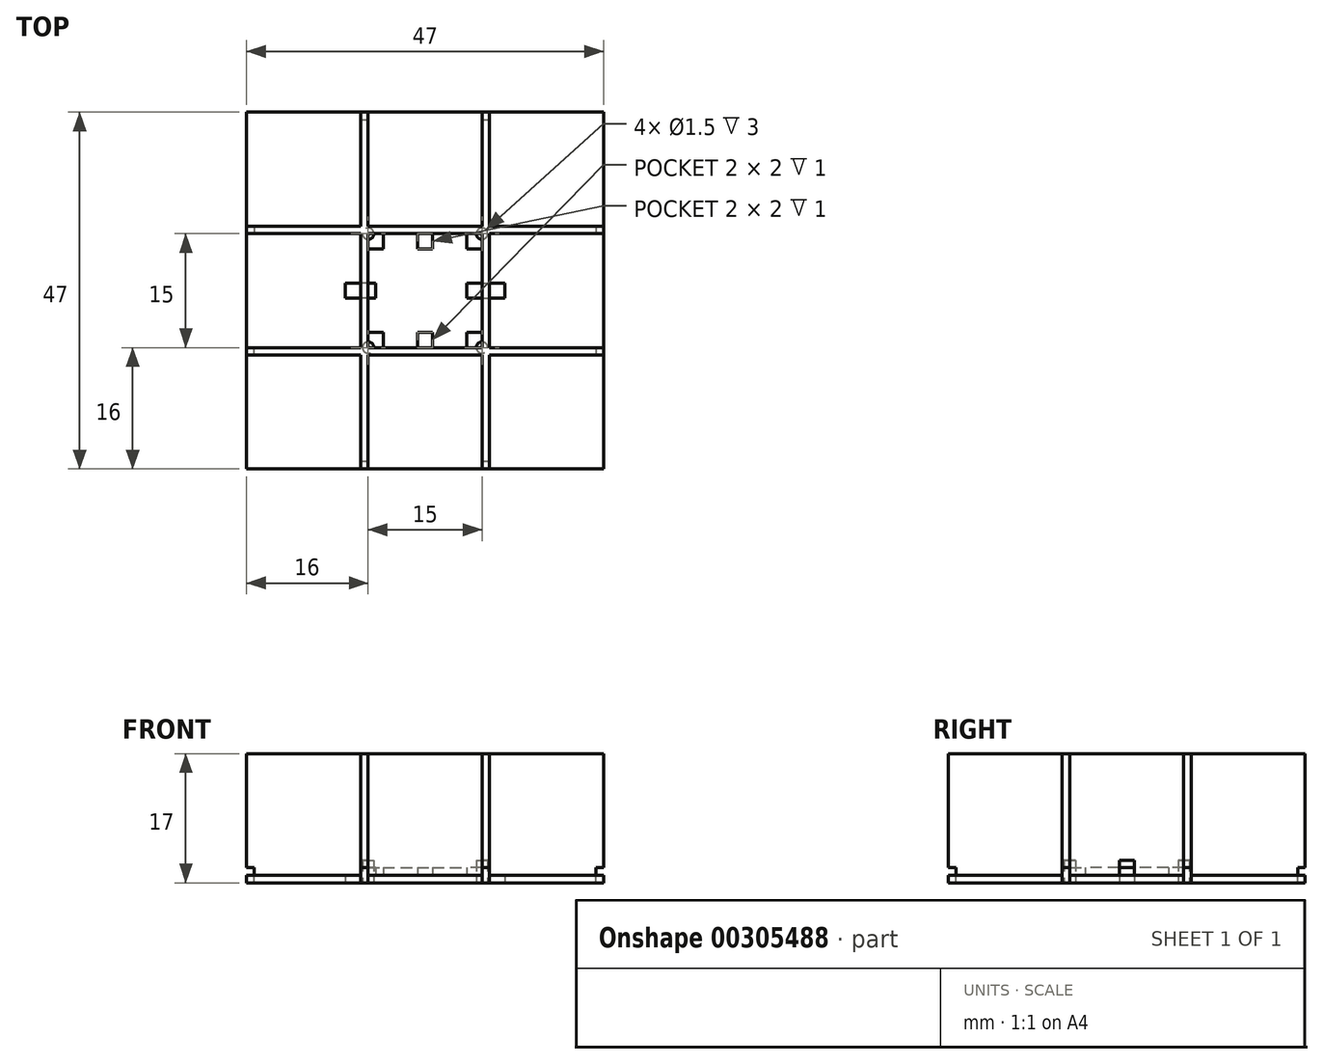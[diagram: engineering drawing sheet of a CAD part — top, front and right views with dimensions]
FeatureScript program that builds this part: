
annotation { "Feature Type Name" : "Feature", "Feature Type Description" : "" }
export const myFeature = defineFeature(function(context is Context, id is Id, definition is map)
    precondition{}
    {
        {
            var Q0;
            Q0=qCreatedBy(makeId("Top.planeOp"),FACE);
            var sketch = newSketch(context, id + "F0", { "sketchPlane" : qUnion([Q0])});
            skLineSegment(sketch, "E0.bottom", {"start": v(-23.5, 23.5) * mm, "end": v(23.5, 23.5) * mm});
            skLineSegment(sketch, "E0.top", {"start": v(-23.5, -23.5) * mm, "end": v(23.5, -23.5) * mm});
            skLineSegment(sketch, "E0.left", {"start": v(-23.5, 23.5) * mm, "end": v(-23.5, -23.5) * mm});
            skLineSegment(sketch, "E0.right", {"start": v(23.5, 23.5) * mm, "end": v(23.5, -23.5) * mm});
            skLineSegment(sketch, "E1", {"start": v(0, 26.11) * mm, "end": v(0, -40.09) * mm, "construction": true});
            skLineSegment(sketch, "E2", {"start": v(37.07, 0) * mm, "end": v(-38.69, 0) * mm, "construction": true});
            skLineSegment(sketch, "E3", {"start": v(-23.5, 8.5) * mm, "end": v(23.5, 8.5) * mm});
            skLineSegment(sketch, "E4", {"start": v(23.5, -8.5) * mm, "end": v(-23.5, -8.5) * mm});
            skLineSegment(sketch, "E5", {"start": v(-8.5, 23.5) * mm, "end": v(-8.5, -23.5) * mm});
            skLineSegment(sketch, "E6", {"start": v(8.5, 23.5) * mm, "end": v(8.5, -23.5) * mm});
            skLineSegment(sketch, "E7.0", {"start": v(-23.5, 7.5) * mm, "end": v(23.5, 7.5) * mm});
            skLineSegment(sketch, "E8.0", {"start": v(23.5, -7.5) * mm, "end": v(-23.5, -7.5) * mm});
            skLineSegment(sketch, "E9.0", {"start": v(-7.5, 23.5) * mm, "end": v(-7.5, -23.5) * mm});
            skLineSegment(sketch, "E10.0", {"start": v(7.5, 23.5) * mm, "end": v(7.5, -23.5) * mm});
            skSolve(sketch);
        }
        {
            var Q0;
            {var subQ0=sQuery(id+"F0.wireOp",EDGE,"E7.0");var subQ1=sQuery(id+"F0.wireOp",EDGE,"E6");var subQ2=makeQuery(id+"F0.imprint","INTERSECT",VERTEX,{"derivedFrom":[subQ1,subQ0]});Q0=makeQuery(id+"F0.imprint","IMPRINT",FACE,{"disambiguationData":[TD([[makeQuery(id+"F0.imprint","IMPRINT",EDGE,{"disambiguationData":[TD([[subQ2,-1.0]])],"derivedFrom":subQ1}),-1.0]])]});}
            var Q1;
            {var subQ0=sQuery(id+"F0.wireOp",EDGE,"E4");var subQ1=sQuery(id+"F0.wireOp",EDGE,"E0.left");var subQ2=makeQuery(id+"F0.imprint","INTERSECT",VERTEX,{"derivedFrom":[subQ1,subQ0]});Q1=makeQuery(id+"F0.imprint","IMPRINT",FACE,{"disambiguationData":[TD([[makeQuery(id+"F0.imprint","IMPRINT",EDGE,{"disambiguationData":[TD([[subQ2,1.0]])],"derivedFrom":subQ1}),1.0]])]});}
            var Q2;
            {var subQ0=sQuery(id+"F0.wireOp",EDGE,"E7.0");var subQ1=sQuery(id+"F0.wireOp",EDGE,"E0.left");var subQ2=makeQuery(id+"F0.imprint","INTERSECT",VERTEX,{"derivedFrom":[subQ1,subQ0]});Q2=makeQuery(id+"F0.imprint","IMPRINT",FACE,{"disambiguationData":[TD([[makeQuery(id+"F0.imprint","IMPRINT",EDGE,{"disambiguationData":[TD([[subQ2,-1.0]])],"derivedFrom":subQ1}),1.0]])]});}
            var Q3;
            {var subQ0=sQuery(id+"F0.wireOp",EDGE,"E6");var subQ1=sQuery(id+"F0.wireOp",EDGE,"E0.top");var subQ2=makeQuery(id+"F0.imprint","INTERSECT",VERTEX,{"derivedFrom":[subQ1,subQ0]});Q3=makeQuery(id+"F0.imprint","IMPRINT",FACE,{"disambiguationData":[TD([[makeQuery(id+"F0.imprint","IMPRINT",EDGE,{"disambiguationData":[TD([[subQ2,1.0]])],"derivedFrom":subQ1}),1.0]])]});}
            var Q4;
            {var subQ0=sQuery(id+"F0.wireOp",EDGE,"E9.0");var subQ1=sQuery(id+"F0.wireOp",EDGE,"E0.top");var subQ2=makeQuery(id+"F0.imprint","INTERSECT",VERTEX,{"derivedFrom":[subQ1,subQ0]});Q4=makeQuery(id+"F0.imprint","IMPRINT",FACE,{"disambiguationData":[TD([[makeQuery(id+"F0.imprint","IMPRINT",EDGE,{"disambiguationData":[TD([[subQ2,-1.0]])],"derivedFrom":subQ1}),1.0]])]});}
            var Q5;
            {var subQ0=sQuery(id+"F0.wireOp",EDGE,"E5");var subQ1=sQuery(id+"F0.wireOp",EDGE,"E0.top");var subQ2=makeQuery(id+"F0.imprint","INTERSECT",VERTEX,{"derivedFrom":[subQ1,subQ0]});Q5=makeQuery(id+"F0.imprint","IMPRINT",FACE,{"disambiguationData":[TD([[makeQuery(id+"F0.imprint","IMPRINT",EDGE,{"disambiguationData":[TD([[subQ2,-1.0]])],"derivedFrom":subQ1}),1.0]])]});}
            var Q6;
            {var subQ0=sQuery(id+"F0.wireOp",EDGE,"E0.right");var subQ1=sQuery(id+"F0.wireOp",EDGE,"E0.top");var subQ2=makeQuery(id+"F0.imprint","INTERSECT",VERTEX,{"derivedFrom":[subQ1,subQ0]});Q6=makeQuery(id+"F0.imprint","IMPRINT",FACE,{"disambiguationData":[TD([[makeQuery(id+"F0.imprint","IMPRINT",EDGE,{"disambiguationData":[TD([[subQ2,1.0]])],"derivedFrom":subQ1}),1.0]])]});}
            var Q7;
            {var subQ0=sQuery(id+"F0.wireOp",EDGE,"E0.left");var subQ1=sQuery(id+"F0.wireOp",EDGE,"E0.top");var subQ2=makeQuery(id+"F0.imprint","INTERSECT",VERTEX,{"derivedFrom":[subQ1,subQ0]});Q7=makeQuery(id+"F0.imprint","IMPRINT",FACE,{"disambiguationData":[TD([[makeQuery(id+"F0.imprint","IMPRINT",EDGE,{"disambiguationData":[TD([[subQ2,-1.0]])],"derivedFrom":subQ1}),1.0]])]});}
            var Q8;
            {var subQ0=sQuery(id+"F0.wireOp",EDGE,"E7.0");var subQ1=sQuery(id+"F0.wireOp",EDGE,"E0.right");var subQ2=makeQuery(id+"F0.imprint","INTERSECT",VERTEX,{"derivedFrom":[subQ1,subQ0]});Q8=makeQuery(id+"F0.imprint","IMPRINT",FACE,{"disambiguationData":[TD([[makeQuery(id+"F0.imprint","IMPRINT",EDGE,{"disambiguationData":[TD([[subQ2,-1.0]])],"derivedFrom":subQ1}),-1.0]])]});}
            var Q9;
            {var subQ0=sQuery(id+"F0.wireOp",EDGE,"E4");var subQ1=sQuery(id+"F0.wireOp",EDGE,"E0.right");var subQ2=makeQuery(id+"F0.imprint","INTERSECT",VERTEX,{"derivedFrom":[subQ1,subQ0]});Q9=makeQuery(id+"F0.imprint","IMPRINT",FACE,{"disambiguationData":[TD([[makeQuery(id+"F0.imprint","IMPRINT",EDGE,{"disambiguationData":[TD([[subQ2,1.0]])],"derivedFrom":subQ1}),-1.0]])]});}
            var Q10;
            {var subQ0=sQuery(id+"F0.wireOp",EDGE,"E10.0");var subQ1=sQuery(id+"F0.wireOp",EDGE,"E4");var subQ2=makeQuery(id+"F0.imprint","INTERSECT",VERTEX,{"derivedFrom":[subQ1,subQ0]});Q10=makeQuery(id+"F0.imprint","IMPRINT",FACE,{"disambiguationData":[TD([[makeQuery(id+"F0.imprint","IMPRINT",EDGE,{"disambiguationData":[TD([[subQ2,-1.0]])],"derivedFrom":subQ1}),-1.0]])]});}
            var Q11;
            {var subQ0=sQuery(id+"F0.wireOp",EDGE,"E7.0");var subQ1=sQuery(id+"F0.wireOp",EDGE,"E5");var subQ2=makeQuery(id+"F0.imprint","INTERSECT",VERTEX,{"derivedFrom":[subQ1,subQ0]});Q11=makeQuery(id+"F0.imprint","IMPRINT",FACE,{"disambiguationData":[TD([[makeQuery(id+"F0.imprint","IMPRINT",EDGE,{"disambiguationData":[TD([[subQ2,-1.0]])],"derivedFrom":subQ1}),1.0]])]});}
            var Q12;
            {var subQ0=sQuery(id+"F0.wireOp",EDGE,"E9.0");var subQ1=sQuery(id+"F0.wireOp",EDGE,"E7.0");var subQ2=makeQuery(id+"F0.imprint","INTERSECT",VERTEX,{"derivedFrom":[subQ1,subQ0]});Q12=makeQuery(id+"F0.imprint","IMPRINT",FACE,{"disambiguationData":[TD([[makeQuery(id+"F0.imprint","IMPRINT",EDGE,{"disambiguationData":[TD([[subQ2,-1.0]])],"derivedFrom":subQ1}),-1.0]])]});}
            var Q13;
            {var subQ0=sQuery(id+"F0.wireOp",EDGE,"E6");var subQ1=sQuery(id+"F0.wireOp",EDGE,"E4");var subQ2=makeQuery(id+"F0.imprint","INTERSECT",VERTEX,{"derivedFrom":[subQ1,subQ0]});Q13=makeQuery(id+"F0.imprint","IMPRINT",FACE,{"disambiguationData":[TD([[makeQuery(id+"F0.imprint","IMPRINT",EDGE,{"disambiguationData":[TD([[subQ2,-1.0]])],"derivedFrom":subQ1}),-1.0]])]});}
            var Q14;
            {var subQ0=sQuery(id+"F0.wireOp",EDGE,"E9.0");var subQ1=sQuery(id+"F0.wireOp",EDGE,"E4");var subQ2=makeQuery(id+"F0.imprint","INTERSECT",VERTEX,{"derivedFrom":[subQ1,subQ0]});Q14=makeQuery(id+"F0.imprint","IMPRINT",FACE,{"disambiguationData":[TD([[makeQuery(id+"F0.imprint","IMPRINT",EDGE,{"disambiguationData":[TD([[subQ2,-1.0]])],"derivedFrom":subQ1}),-1.0]])]});}
            var Q15;
            {var subQ0=sQuery(id+"F0.wireOp",EDGE,"E5");var subQ1=sQuery(id+"F0.wireOp",EDGE,"E3");var subQ2=makeQuery(id+"F0.imprint","INTERSECT",VERTEX,{"derivedFrom":[subQ1,subQ0]});Q15=makeQuery(id+"F0.imprint","IMPRINT",FACE,{"disambiguationData":[TD([[makeQuery(id+"F0.imprint","IMPRINT",EDGE,{"disambiguationData":[TD([[subQ2,-1.0]])],"derivedFrom":subQ1}),-1.0]])]});}
            var Q16;
            {var subQ0=sQuery(id+"F0.wireOp",EDGE,"E3");var subQ1=sQuery(id+"F0.wireOp",EDGE,"E0.left");var subQ2=makeQuery(id+"F0.imprint","INTERSECT",VERTEX,{"derivedFrom":[subQ1,subQ0]});Q16=makeQuery(id+"F0.imprint","IMPRINT",FACE,{"disambiguationData":[TD([[makeQuery(id+"F0.imprint","IMPRINT",EDGE,{"disambiguationData":[TD([[subQ2,-1.0]])],"derivedFrom":subQ1}),1.0]])]});}
            var Q17;
            {var subQ0=sQuery(id+"F0.wireOp",EDGE,"E6");var subQ1=sQuery(id+"F0.wireOp",EDGE,"E0.bottom");var subQ2=makeQuery(id+"F0.imprint","INTERSECT",VERTEX,{"derivedFrom":[subQ1,subQ0]});Q17=makeQuery(id+"F0.imprint","IMPRINT",FACE,{"disambiguationData":[TD([[makeQuery(id+"F0.imprint","IMPRINT",EDGE,{"disambiguationData":[TD([[subQ2,1.0]])],"derivedFrom":subQ1}),-1.0]])]});}
            var Q18;
            {var subQ0=sQuery(id+"F0.wireOp",EDGE,"E9.0");var subQ1=sQuery(id+"F0.wireOp",EDGE,"E0.bottom");var subQ2=makeQuery(id+"F0.imprint","INTERSECT",VERTEX,{"derivedFrom":[subQ1,subQ0]});Q18=makeQuery(id+"F0.imprint","IMPRINT",FACE,{"disambiguationData":[TD([[makeQuery(id+"F0.imprint","IMPRINT",EDGE,{"disambiguationData":[TD([[subQ2,-1.0]])],"derivedFrom":subQ1}),-1.0]])]});}
            var Q19;
            {var subQ0=sQuery(id+"F0.wireOp",EDGE,"E5");var subQ1=sQuery(id+"F0.wireOp",EDGE,"E0.bottom");var subQ2=makeQuery(id+"F0.imprint","INTERSECT",VERTEX,{"derivedFrom":[subQ1,subQ0]});Q19=makeQuery(id+"F0.imprint","IMPRINT",FACE,{"disambiguationData":[TD([[makeQuery(id+"F0.imprint","IMPRINT",EDGE,{"disambiguationData":[TD([[subQ2,-1.0]])],"derivedFrom":subQ1}),-1.0]])]});}
            var Q20;
            {var subQ0=sQuery(id+"F0.wireOp",EDGE,"E0.right");var subQ1=sQuery(id+"F0.wireOp",EDGE,"E0.bottom");var subQ2=makeQuery(id+"F0.imprint","INTERSECT",VERTEX,{"derivedFrom":[subQ1,subQ0]});Q20=makeQuery(id+"F0.imprint","IMPRINT",FACE,{"disambiguationData":[TD([[makeQuery(id+"F0.imprint","IMPRINT",EDGE,{"disambiguationData":[TD([[subQ2,1.0]])],"derivedFrom":subQ1}),-1.0]])]});}
            var Q21;
            {var subQ0=sQuery(id+"F0.wireOp",EDGE,"E3");var subQ1=sQuery(id+"F0.wireOp",EDGE,"E0.right");var subQ2=makeQuery(id+"F0.imprint","INTERSECT",VERTEX,{"derivedFrom":[subQ1,subQ0]});Q21=makeQuery(id+"F0.imprint","IMPRINT",FACE,{"disambiguationData":[TD([[makeQuery(id+"F0.imprint","IMPRINT",EDGE,{"disambiguationData":[TD([[subQ2,-1.0]])],"derivedFrom":subQ1}),-1.0]])]});}
            var Q22;
            {var subQ0=sQuery(id+"F0.wireOp",EDGE,"E0.left");var subQ1=sQuery(id+"F0.wireOp",EDGE,"E0.bottom");var subQ2=makeQuery(id+"F0.imprint","INTERSECT",VERTEX,{"derivedFrom":[subQ1,subQ0]});Q22=makeQuery(id+"F0.imprint","IMPRINT",FACE,{"disambiguationData":[TD([[makeQuery(id+"F0.imprint","IMPRINT",EDGE,{"disambiguationData":[TD([[subQ2,-1.0]])],"derivedFrom":subQ1}),-1.0]])]});}
            var Q23;
            {var subQ0=sQuery(id+"F0.wireOp",EDGE,"E10.0");var subQ1=sQuery(id+"F0.wireOp",EDGE,"E3");var subQ2=makeQuery(id+"F0.imprint","INTERSECT",VERTEX,{"derivedFrom":[subQ1,subQ0]});Q23=makeQuery(id+"F0.imprint","IMPRINT",FACE,{"disambiguationData":[TD([[makeQuery(id+"F0.imprint","IMPRINT",EDGE,{"disambiguationData":[TD([[subQ2,-1.0]])],"derivedFrom":subQ1}),-1.0]])]});}
            var Q24;
            {var subQ0=sQuery(id+"F0.wireOp",EDGE,"E9.0");var subQ1=sQuery(id+"F0.wireOp",EDGE,"E3");var subQ2=makeQuery(id+"F0.imprint","INTERSECT",VERTEX,{"derivedFrom":[subQ1,subQ0]});Q24=makeQuery(id+"F0.imprint","IMPRINT",FACE,{"disambiguationData":[TD([[makeQuery(id+"F0.imprint","IMPRINT",EDGE,{"disambiguationData":[TD([[subQ2,-1.0]])],"derivedFrom":subQ1}),-1.0]])]});}
            extrude(context, id + "F1", {"entities" : qUnion([Q0, Q1, Q2, Q3, Q4, Q5, Q6, Q7, Q8, Q9, Q10, Q11, Q12, Q13, Q14, Q15, Q16, Q17, Q18, Q19, Q20, Q21, Q22, Q23, Q24]), "oppositeDirection" : true, "depth" : 1 * mm});
        }
        {
            var Q0;
            {var subQ0=sQuery(id+"F0.wireOp",EDGE,"E9.0");var subQ1=sQuery(id+"F0.wireOp",EDGE,"E4");var subQ2=makeQuery(id+"F0.imprint","INTERSECT",VERTEX,{"derivedFrom":[subQ1,subQ0]});Q0=makeQuery(id+"F0.imprint","IMPRINT",FACE,{"disambiguationData":[TD([[makeQuery(id+"F0.imprint","IMPRINT",EDGE,{"disambiguationData":[TD([[subQ2,-1.0]])],"derivedFrom":subQ1}),-1.0]])]});}
            var Q1;
            {var subQ0=sQuery(id+"F0.wireOp",EDGE,"E6");var subQ1=sQuery(id+"F0.wireOp",EDGE,"E4");var subQ2=makeQuery(id+"F0.imprint","INTERSECT",VERTEX,{"derivedFrom":[subQ1,subQ0]});Q1=makeQuery(id+"F0.imprint","IMPRINT",FACE,{"disambiguationData":[TD([[makeQuery(id+"F0.imprint","IMPRINT",EDGE,{"disambiguationData":[TD([[subQ2,-1.0]])],"derivedFrom":subQ1}),-1.0]])]});}
            var Q2;
            {var subQ0=sQuery(id+"F0.wireOp",EDGE,"E5");var subQ1=sQuery(id+"F0.wireOp",EDGE,"E3");var subQ2=makeQuery(id+"F0.imprint","INTERSECT",VERTEX,{"derivedFrom":[subQ1,subQ0]});Q2=makeQuery(id+"F0.imprint","IMPRINT",FACE,{"disambiguationData":[TD([[makeQuery(id+"F0.imprint","IMPRINT",EDGE,{"disambiguationData":[TD([[subQ2,-1.0]])],"derivedFrom":subQ1}),-1.0]])]});}
            var Q3;
            {var subQ0=sQuery(id+"F0.wireOp",EDGE,"E10.0");var subQ1=sQuery(id+"F0.wireOp",EDGE,"E3");var subQ2=makeQuery(id+"F0.imprint","INTERSECT",VERTEX,{"derivedFrom":[subQ1,subQ0]});Q3=makeQuery(id+"F0.imprint","IMPRINT",FACE,{"disambiguationData":[TD([[makeQuery(id+"F0.imprint","IMPRINT",EDGE,{"disambiguationData":[TD([[subQ2,-1.0]])],"derivedFrom":subQ1}),-1.0]])]});}
            var Q4;
            {var subQ0=sQuery(id+"F0.wireOp",EDGE,"E3");var subQ1=sQuery(id+"F0.wireOp",EDGE,"E0.right");var subQ2=makeQuery(id+"F0.imprint","INTERSECT",VERTEX,{"derivedFrom":[subQ1,subQ0]});Q4=makeQuery(id+"F0.imprint","IMPRINT",FACE,{"disambiguationData":[TD([[makeQuery(id+"F0.imprint","IMPRINT",EDGE,{"disambiguationData":[TD([[subQ2,-1.0]])],"derivedFrom":subQ1}),-1.0]])]});}
            var Q5;
            {var subQ0=sQuery(id+"F0.wireOp",EDGE,"E6");var subQ1=sQuery(id+"F0.wireOp",EDGE,"E0.bottom");var subQ2=makeQuery(id+"F0.imprint","INTERSECT",VERTEX,{"derivedFrom":[subQ1,subQ0]});Q5=makeQuery(id+"F0.imprint","IMPRINT",FACE,{"disambiguationData":[TD([[makeQuery(id+"F0.imprint","IMPRINT",EDGE,{"disambiguationData":[TD([[subQ2,1.0]])],"derivedFrom":subQ1}),-1.0]])]});}
            var Q6;
            {var subQ0=sQuery(id+"F0.wireOp",EDGE,"E5");var subQ1=sQuery(id+"F0.wireOp",EDGE,"E0.bottom");var subQ2=makeQuery(id+"F0.imprint","INTERSECT",VERTEX,{"derivedFrom":[subQ1,subQ0]});Q6=makeQuery(id+"F0.imprint","IMPRINT",FACE,{"disambiguationData":[TD([[makeQuery(id+"F0.imprint","IMPRINT",EDGE,{"disambiguationData":[TD([[subQ2,-1.0]])],"derivedFrom":subQ1}),-1.0]])]});}
            var Q7;
            {var subQ0=sQuery(id+"F0.wireOp",EDGE,"E9.0");var subQ1=sQuery(id+"F0.wireOp",EDGE,"E3");var subQ2=makeQuery(id+"F0.imprint","INTERSECT",VERTEX,{"derivedFrom":[subQ1,subQ0]});Q7=makeQuery(id+"F0.imprint","IMPRINT",FACE,{"disambiguationData":[TD([[makeQuery(id+"F0.imprint","IMPRINT",EDGE,{"disambiguationData":[TD([[subQ2,-1.0]])],"derivedFrom":subQ1}),-1.0]])]});}
            var Q8;
            {var subQ0=sQuery(id+"F0.wireOp",EDGE,"E3");var subQ1=sQuery(id+"F0.wireOp",EDGE,"E0.left");var subQ2=makeQuery(id+"F0.imprint","INTERSECT",VERTEX,{"derivedFrom":[subQ1,subQ0]});Q8=makeQuery(id+"F0.imprint","IMPRINT",FACE,{"disambiguationData":[TD([[makeQuery(id+"F0.imprint","IMPRINT",EDGE,{"disambiguationData":[TD([[subQ2,-1.0]])],"derivedFrom":subQ1}),1.0]])]});}
            var Q9;
            {var subQ0=sQuery(id+"F0.wireOp",EDGE,"E7.0");var subQ1=sQuery(id+"F0.wireOp",EDGE,"E5");var subQ2=makeQuery(id+"F0.imprint","INTERSECT",VERTEX,{"derivedFrom":[subQ1,subQ0]});Q9=makeQuery(id+"F0.imprint","IMPRINT",FACE,{"disambiguationData":[TD([[makeQuery(id+"F0.imprint","IMPRINT",EDGE,{"disambiguationData":[TD([[subQ2,-1.0]])],"derivedFrom":subQ1}),1.0]])]});}
            var Q10;
            {var subQ0=sQuery(id+"F0.wireOp",EDGE,"E4");var subQ1=sQuery(id+"F0.wireOp",EDGE,"E0.left");var subQ2=makeQuery(id+"F0.imprint","INTERSECT",VERTEX,{"derivedFrom":[subQ1,subQ0]});Q10=makeQuery(id+"F0.imprint","IMPRINT",FACE,{"disambiguationData":[TD([[makeQuery(id+"F0.imprint","IMPRINT",EDGE,{"disambiguationData":[TD([[subQ2,1.0]])],"derivedFrom":subQ1}),1.0]])]});}
            var Q11;
            {var subQ0=sQuery(id+"F0.wireOp",EDGE,"E10.0");var subQ1=sQuery(id+"F0.wireOp",EDGE,"E4");var subQ2=makeQuery(id+"F0.imprint","INTERSECT",VERTEX,{"derivedFrom":[subQ1,subQ0]});Q11=makeQuery(id+"F0.imprint","IMPRINT",FACE,{"disambiguationData":[TD([[makeQuery(id+"F0.imprint","IMPRINT",EDGE,{"disambiguationData":[TD([[subQ2,-1.0]])],"derivedFrom":subQ1}),-1.0]])]});}
            var Q12;
            {var subQ0=sQuery(id+"F0.wireOp",EDGE,"E4");var subQ1=sQuery(id+"F0.wireOp",EDGE,"E0.right");var subQ2=makeQuery(id+"F0.imprint","INTERSECT",VERTEX,{"derivedFrom":[subQ1,subQ0]});Q12=makeQuery(id+"F0.imprint","IMPRINT",FACE,{"disambiguationData":[TD([[makeQuery(id+"F0.imprint","IMPRINT",EDGE,{"disambiguationData":[TD([[subQ2,1.0]])],"derivedFrom":subQ1}),-1.0]])]});}
            var Q13;
            {var subQ0=sQuery(id+"F0.wireOp",EDGE,"E6");var subQ1=sQuery(id+"F0.wireOp",EDGE,"E0.top");var subQ2=makeQuery(id+"F0.imprint","INTERSECT",VERTEX,{"derivedFrom":[subQ1,subQ0]});Q13=makeQuery(id+"F0.imprint","IMPRINT",FACE,{"disambiguationData":[TD([[makeQuery(id+"F0.imprint","IMPRINT",EDGE,{"disambiguationData":[TD([[subQ2,1.0]])],"derivedFrom":subQ1}),1.0]])]});}
            var Q14;
            {var subQ0=sQuery(id+"F0.wireOp",EDGE,"E5");var subQ1=sQuery(id+"F0.wireOp",EDGE,"E0.top");var subQ2=makeQuery(id+"F0.imprint","INTERSECT",VERTEX,{"derivedFrom":[subQ1,subQ0]});Q14=makeQuery(id+"F0.imprint","IMPRINT",FACE,{"disambiguationData":[TD([[makeQuery(id+"F0.imprint","IMPRINT",EDGE,{"disambiguationData":[TD([[subQ2,-1.0]])],"derivedFrom":subQ1}),1.0]])]});}
            var Q15;
            {var subQ0=sQuery(id+"F0.wireOp",EDGE,"E7.0");var subQ1=sQuery(id+"F0.wireOp",EDGE,"E6");var subQ2=makeQuery(id+"F0.imprint","INTERSECT",VERTEX,{"derivedFrom":[subQ1,subQ0]});Q15=makeQuery(id+"F0.imprint","IMPRINT",FACE,{"disambiguationData":[TD([[makeQuery(id+"F0.imprint","IMPRINT",EDGE,{"disambiguationData":[TD([[subQ2,-1.0]])],"derivedFrom":subQ1}),-1.0]])]});}
            extrude(context, id + "F2", {"entities" : qUnion([Q0, Q1, Q2, Q3, Q4, Q5, Q6, Q7, Q8, Q9, Q10, Q11, Q12, Q13, Q14, Q15]), "operationType" : NewBodyOperationType.ADD, "depth" : 16 * mm});
        }
        {
            var Q0;
            Q0=makeQuery(id+"F1.opExtrude","CAP_FACE",FACE,{"disambiguationData":[OSD([sQuery(id+"F0.wireOp",EDGE,"E0.bottom"),sQuery(id+"F0.wireOp",EDGE,"E0.top"),sQuery(id+"F0.wireOp",EDGE,"E0.left"),sQuery(id+"F0.wireOp",EDGE,"E0.right")])],"isStart":false});
            var sketch = newSketch(context, id + "F3", { "sketchPlane" : qUnion([Q0])});
            skLineSegment(sketch, "E11.bottom", {"start": v(-7.5, 7.5) * mm, "end": v(7.5, 7.5) * mm});
            skLineSegment(sketch, "E11.top", {"start": v(-7.5, -7.5) * mm, "end": v(7.5, -7.5) * mm});
            skLineSegment(sketch, "E11.left", {"start": v(-7.5, 7.5) * mm, "end": v(-7.5, -7.5) * mm});
            skLineSegment(sketch, "E11.right", {"start": v(7.5, 7.5) * mm, "end": v(7.5, -7.5) * mm});
            skLineSegment(sketch, "E12.0", {"start": v(7.5, 8.5) * mm, "end": v(-7.5, 8.5) * mm, "construction": true});
            skLineSegment(sketch, "E13", {"start": v(0, 19.4) * mm, "end": v(0, -17.52) * mm, "construction": true});
            skLineSegment(sketch, "E14", {"start": v(14.3, 0) * mm, "end": v(-21.62, 0) * mm, "construction": true});
            skPoint(sketch, "E14.endSnap0", {"position": v(-23.5, 0) * mm});
            skLineSegment(sketch, "E15.0", {"start": v(10.5, 10.5) * mm, "end": v(10.5, -10.5) * mm});
            skLineSegment(sketch, "E15.1", {"start": v(-10.5, 10.5) * mm, "end": v(10.5, 10.5) * mm});
            skLineSegment(sketch, "E15.2", {"start": v(-10.5, 10.5) * mm, "end": v(-10.5, -10.5) * mm});
            skLineSegment(sketch, "E15.3", {"start": v(-10.5, -10.5) * mm, "end": v(10.5, -10.5) * mm});
            skLineSegment(sketch, "E16.bottom", {"start": v(-7.5, 1) * mm, "end": v(-10.5, 1) * mm});
            skLineSegment(sketch, "E16.top", {"start": v(-7.5, -1) * mm, "end": v(-10.5, -1) * mm});
            skLineSegment(sketch, "E16.left", {"start": v(-7.5, 1) * mm, "end": v(-7.5, -1) * mm});
            skLineSegment(sketch, "E16.right", {"start": v(-10.5, 1) * mm, "end": v(-10.5, -1) * mm});
            skLineSegment(sketch, "E17.bottom", {"start": v(-1, 10.5) * mm, "end": v(1, 10.5) * mm});
            skLineSegment(sketch, "E17.top", {"start": v(-1, 7.5) * mm, "end": v(1, 7.5) * mm});
            skLineSegment(sketch, "E17.left", {"start": v(-1, 10.5) * mm, "end": v(-1, 7.5) * mm});
            skLineSegment(sketch, "E17.right", {"start": v(1, 10.5) * mm, "end": v(1, 7.5) * mm});
            skLineSegment(sketch, "E18.bottom", {"start": v(7.5, 1) * mm, "end": v(10.5, 1) * mm});
            skLineSegment(sketch, "E18.top", {"start": v(7.5, -1) * mm, "end": v(10.5, -1) * mm});
            skLineSegment(sketch, "E18.left", {"start": v(7.5, 1) * mm, "end": v(7.5, -1) * mm});
            skLineSegment(sketch, "E18.right", {"start": v(10.5, 1) * mm, "end": v(10.5, -1) * mm});
            skLineSegment(sketch, "E19.bottom", {"start": v(1, -7.5) * mm, "end": v(-1, -7.5) * mm});
            skLineSegment(sketch, "E19.top", {"start": v(1, -10.5) * mm, "end": v(-1, -10.5) * mm});
            skLineSegment(sketch, "E19.left", {"start": v(1, -7.5) * mm, "end": v(1, -10.5) * mm});
            skLineSegment(sketch, "E19.right", {"start": v(-1, -7.5) * mm, "end": v(-1, -10.5) * mm});
            skLineSegment(sketch, "E20.bottom", {"start": v(-10.5, 10.5) * mm, "end": v(-7.5, 10.5) * mm});
            skLineSegment(sketch, "E20.top", {"start": v(-10.5, 7.5) * mm, "end": v(-7.5, 7.5) * mm});
            skLineSegment(sketch, "E20.left", {"start": v(-10.5, 10.5) * mm, "end": v(-10.5, 7.5) * mm});
            skLineSegment(sketch, "E20.right", {"start": v(-7.5, 10.5) * mm, "end": v(-7.5, 7.5) * mm});
            skLineSegment(sketch, "E21.bottom", {"start": v(10.5, 10.5) * mm, "end": v(7.5, 10.5) * mm});
            skLineSegment(sketch, "E21.top", {"start": v(10.5, 7.5) * mm, "end": v(7.5, 7.5) * mm});
            skLineSegment(sketch, "E21.left", {"start": v(10.5, 10.5) * mm, "end": v(10.5, 7.5) * mm});
            skLineSegment(sketch, "E21.right", {"start": v(7.5, 10.5) * mm, "end": v(7.5, 7.5) * mm});
            skLineSegment(sketch, "E22.bottom", {"start": v(10.5, -10.5) * mm, "end": v(7.5, -10.5) * mm});
            skLineSegment(sketch, "E22.top", {"start": v(10.5, -7.5) * mm, "end": v(7.5, -7.5) * mm});
            skLineSegment(sketch, "E22.left", {"start": v(10.5, -10.5) * mm, "end": v(10.5, -7.5) * mm});
            skLineSegment(sketch, "E22.right", {"start": v(7.5, -10.5) * mm, "end": v(7.5, -7.5) * mm});
            skLineSegment(sketch, "E23.bottom", {"start": v(-10.5, -10.5) * mm, "end": v(-7.5, -10.5) * mm});
            skLineSegment(sketch, "E23.top", {"start": v(-10.5, -7.5) * mm, "end": v(-7.5, -7.5) * mm});
            skLineSegment(sketch, "E23.left", {"start": v(-10.5, -10.5) * mm, "end": v(-10.5, -7.5) * mm});
            skLineSegment(sketch, "E23.right", {"start": v(-7.5, -10.5) * mm, "end": v(-7.5, -7.5) * mm});
            skCircle(sketch, "E24", {"center": v(-7.5, -7.5) * mm, "radius": 0.75 * mm});
            skCircle(sketch, "E25", {"center": v(7.5, -7.5) * mm, "radius": 0.75 * mm});
            skCircle(sketch, "E26", {"center": v(7.5, 7.5) * mm, "radius": 0.75 * mm});
            skCircle(sketch, "E27", {"center": v(-7.5, 7.5) * mm, "radius": 0.75 * mm});
            skSolve(sketch);
        }
        {
            var Q0;
            Q0=makeQuery(id+"F3.imprint","IMPRINT",FACE,{"disambiguationData":[TD([[makeQuery(id+"F3.imprint","IMPRINT",EDGE,{"derivedFrom":sQuery(id+"F3.wireOp",EDGE,"E17.bottom")}),-1.0]])]});
            var Q1;
            Q1=makeQuery(id+"F3.imprint","IMPRINT",FACE,{"disambiguationData":[TD([[makeQuery(id+"F3.imprint","IMPRINT",EDGE,{"derivedFrom":sQuery(id+"F3.wireOp",EDGE,"E18.bottom")}),-1.0]])]});
            var Q2;
            Q2=makeQuery(id+"F3.imprint","IMPRINT",FACE,{"disambiguationData":[TD([[makeQuery(id+"F3.imprint","IMPRINT",EDGE,{"derivedFrom":sQuery(id+"F3.wireOp",EDGE,"E19.bottom")}),1.0]])]});
            var Q3;
            Q3=makeQuery(id+"F3.imprint","IMPRINT",FACE,{"disambiguationData":[TD([[makeQuery(id+"F3.imprint","IMPRINT",EDGE,{"derivedFrom":sQuery(id+"F3.wireOp",EDGE,"E16.bottom")}),1.0]])]});
            var Q4;
            {var subQ1=sQuery(id+"F3.wireOp",EDGE,"E16.left");Q4=makeQuery(id+"F3.imprint","IMPRINT",FACE,{"disambiguationData":[TD([[makeQuery(id+"F3.imprint","IMPRINT",EDGE,{"derivedFrom":subQ1}),1.0]])]});}
            var Q5;
            {var subQ1=sQuery(id+"F3.wireOp",EDGE,"E23.bottom");Q5=makeQuery(id+"F3.imprint","IMPRINT",FACE,{"disambiguationData":[TD([[makeQuery(id+"F3.imprint","IMPRINT",EDGE,{"derivedFrom":subQ1}),1.0]])]});}
            var Q6;
            {var subQ1=sQuery(id+"F3.wireOp",EDGE,"E22.bottom");Q6=makeQuery(id+"F3.imprint","IMPRINT",FACE,{"disambiguationData":[TD([[makeQuery(id+"F3.imprint","IMPRINT",EDGE,{"derivedFrom":subQ1}),-1.0]])]});}
            var Q7;
            {var subQ1=sQuery(id+"F3.wireOp",EDGE,"E21.bottom");Q7=makeQuery(id+"F3.imprint","IMPRINT",FACE,{"disambiguationData":[TD([[makeQuery(id+"F3.imprint","IMPRINT",EDGE,{"derivedFrom":subQ1}),1.0]])]});}
            var Q8;
            {var subQ1=sQuery(id+"F3.wireOp",EDGE,"E20.bottom");Q8=makeQuery(id+"F3.imprint","IMPRINT",FACE,{"disambiguationData":[TD([[makeQuery(id+"F3.imprint","IMPRINT",EDGE,{"derivedFrom":subQ1}),-1.0]])]});}
            var Q9;
            {var subQ1=sQuery(id+"F3.wireOp",EDGE,"E11.bottom");var subQ3=sQuery(id+"F3.wireOp",EDGE,"E27");var subQ4=makeQuery(id+"F3.imprint","INTERSECT",VERTEX,{"derivedFrom":[subQ1,subQ3]});Q9=makeQuery(id+"F3.imprint","IMPRINT",FACE,{"disambiguationData":[TD([[makeQuery(id+"F3.imprint","IMPRINT",EDGE,{"disambiguationData":[TD([[subQ4,-1.0]])],"derivedFrom":subQ3}),1.0]])]});}
            var Q10;
            {var subQ1=sQuery(id+"F3.wireOp",EDGE,"E11.left");var subQ3=sQuery(id+"F3.wireOp",EDGE,"E27");var subQ4=makeQuery(id+"F3.imprint","INTERSECT",VERTEX,{"derivedFrom":[subQ1,subQ3]});Q10=makeQuery(id+"F3.imprint","IMPRINT",FACE,{"disambiguationData":[TD([[makeQuery(id+"F3.imprint","IMPRINT",EDGE,{"disambiguationData":[TD([[subQ4,1.0]])],"derivedFrom":subQ3}),1.0]])]});}
            var Q11;
            {var subQ1=sQuery(id+"F3.wireOp",EDGE,"E11.bottom");var subQ3=sQuery(id+"F3.wireOp",EDGE,"E26");var subQ4=makeQuery(id+"F3.imprint","INTERSECT",VERTEX,{"derivedFrom":[subQ1,subQ3]});Q11=makeQuery(id+"F3.imprint","IMPRINT",FACE,{"disambiguationData":[TD([[makeQuery(id+"F3.imprint","IMPRINT",EDGE,{"disambiguationData":[TD([[subQ4,-1.0]])],"derivedFrom":subQ3}),1.0]])]});}
            var Q12;
            {var subQ1=sQuery(id+"F3.wireOp",EDGE,"E21.top");var subQ3=sQuery(id+"F3.wireOp",EDGE,"E26");var subQ4=makeQuery(id+"F3.imprint","INTERSECT",VERTEX,{"derivedFrom":[subQ1,subQ3]});Q12=makeQuery(id+"F3.imprint","IMPRINT",FACE,{"disambiguationData":[TD([[makeQuery(id+"F3.imprint","IMPRINT",EDGE,{"disambiguationData":[TD([[subQ4,-1.0]])],"derivedFrom":subQ3}),1.0]])]});}
            var Q13;
            {var subQ1=sQuery(id+"F3.wireOp",EDGE,"E11.bottom");var subQ3=sQuery(id+"F3.wireOp",EDGE,"E26");var subQ4=makeQuery(id+"F3.imprint","INTERSECT",VERTEX,{"derivedFrom":[subQ1,subQ3]});Q13=makeQuery(id+"F3.imprint","IMPRINT",FACE,{"disambiguationData":[TD([[makeQuery(id+"F3.imprint","IMPRINT",EDGE,{"disambiguationData":[TD([[subQ4,1.0]])],"derivedFrom":subQ3}),1.0]])]});}
            var Q14;
            {var subQ1=sQuery(id+"F3.wireOp",EDGE,"E11.right");var subQ3=sQuery(id+"F3.wireOp",EDGE,"E26");var subQ4=makeQuery(id+"F3.imprint","INTERSECT",VERTEX,{"derivedFrom":[subQ1,subQ3]});Q14=makeQuery(id+"F3.imprint","IMPRINT",FACE,{"disambiguationData":[TD([[makeQuery(id+"F3.imprint","IMPRINT",EDGE,{"disambiguationData":[TD([[subQ4,-1.0]])],"derivedFrom":subQ3}),1.0]])]});}
            var Q15;
            {var subQ1=sQuery(id+"F3.wireOp",EDGE,"E11.top");var subQ3=sQuery(id+"F3.wireOp",EDGE,"E25");var subQ4=makeQuery(id+"F3.imprint","INTERSECT",VERTEX,{"derivedFrom":[subQ1,subQ3]});Q15=makeQuery(id+"F3.imprint","IMPRINT",FACE,{"disambiguationData":[TD([[makeQuery(id+"F3.imprint","IMPRINT",EDGE,{"disambiguationData":[TD([[subQ4,1.0]])],"derivedFrom":subQ3}),1.0]])]});}
            var Q16;
            {var subQ1=sQuery(id+"F3.wireOp",EDGE,"E22.top");var subQ3=sQuery(id+"F3.wireOp",EDGE,"E25");var subQ4=makeQuery(id+"F3.imprint","INTERSECT",VERTEX,{"derivedFrom":[subQ1,subQ3]});Q16=makeQuery(id+"F3.imprint","IMPRINT",FACE,{"disambiguationData":[TD([[makeQuery(id+"F3.imprint","IMPRINT",EDGE,{"disambiguationData":[TD([[subQ4,1.0]])],"derivedFrom":subQ3}),1.0]])]});}
            var Q17;
            {var subQ1=sQuery(id+"F3.wireOp",EDGE,"E11.right");var subQ3=sQuery(id+"F3.wireOp",EDGE,"E25");var subQ4=makeQuery(id+"F3.imprint","INTERSECT",VERTEX,{"derivedFrom":[subQ1,subQ3]});Q17=makeQuery(id+"F3.imprint","IMPRINT",FACE,{"disambiguationData":[TD([[makeQuery(id+"F3.imprint","IMPRINT",EDGE,{"disambiguationData":[TD([[subQ4,1.0]])],"derivedFrom":subQ3}),1.0]])]});}
            var Q18;
            {var subQ1=sQuery(id+"F3.wireOp",EDGE,"E11.top");var subQ3=sQuery(id+"F3.wireOp",EDGE,"E25");var subQ4=makeQuery(id+"F3.imprint","INTERSECT",VERTEX,{"derivedFrom":[subQ1,subQ3]});Q18=makeQuery(id+"F3.imprint","IMPRINT",FACE,{"disambiguationData":[TD([[makeQuery(id+"F3.imprint","IMPRINT",EDGE,{"disambiguationData":[TD([[subQ4,-1.0]])],"derivedFrom":subQ3}),1.0]])]});}
            var Q19;
            {var subQ1=sQuery(id+"F3.wireOp",EDGE,"E23.top");var subQ3=sQuery(id+"F3.wireOp",EDGE,"E24");var subQ4=makeQuery(id+"F3.imprint","INTERSECT",VERTEX,{"derivedFrom":[subQ1,subQ3]});Q19=makeQuery(id+"F3.imprint","IMPRINT",FACE,{"disambiguationData":[TD([[makeQuery(id+"F3.imprint","IMPRINT",EDGE,{"disambiguationData":[TD([[subQ4,-1.0]])],"derivedFrom":subQ3}),1.0]])]});}
            var Q20;
            {var subQ1=sQuery(id+"F3.wireOp",EDGE,"E11.top");var subQ3=sQuery(id+"F3.wireOp",EDGE,"E24");var subQ4=makeQuery(id+"F3.imprint","INTERSECT",VERTEX,{"derivedFrom":[subQ1,subQ3]});Q20=makeQuery(id+"F3.imprint","IMPRINT",FACE,{"disambiguationData":[TD([[makeQuery(id+"F3.imprint","IMPRINT",EDGE,{"disambiguationData":[TD([[subQ4,-1.0]])],"derivedFrom":subQ3}),1.0]])]});}
            var Q21;
            {var subQ1=sQuery(id+"F3.wireOp",EDGE,"E11.left");var subQ3=sQuery(id+"F3.wireOp",EDGE,"E24");var subQ4=makeQuery(id+"F3.imprint","INTERSECT",VERTEX,{"derivedFrom":[subQ1,subQ3]});Q21=makeQuery(id+"F3.imprint","IMPRINT",FACE,{"disambiguationData":[TD([[makeQuery(id+"F3.imprint","IMPRINT",EDGE,{"disambiguationData":[TD([[subQ4,-1.0]])],"derivedFrom":subQ3}),1.0]])]});}
            var Q22;
            {var subQ1=sQuery(id+"F3.wireOp",EDGE,"E11.top");var subQ3=sQuery(id+"F3.wireOp",EDGE,"E24");var subQ4=makeQuery(id+"F3.imprint","INTERSECT",VERTEX,{"derivedFrom":[subQ1,subQ3]});Q22=makeQuery(id+"F3.imprint","IMPRINT",FACE,{"disambiguationData":[TD([[makeQuery(id+"F3.imprint","IMPRINT",EDGE,{"disambiguationData":[TD([[subQ4,1.0]])],"derivedFrom":subQ3}),1.0]])]});}
            var Q23;
            {var subQ1=sQuery(id+"F3.wireOp",EDGE,"E20.top");var subQ3=sQuery(id+"F3.wireOp",EDGE,"E27");var subQ4=makeQuery(id+"F3.imprint","INTERSECT",VERTEX,{"derivedFrom":[subQ1,subQ3]});Q23=makeQuery(id+"F3.imprint","IMPRINT",FACE,{"disambiguationData":[TD([[makeQuery(id+"F3.imprint","IMPRINT",EDGE,{"disambiguationData":[TD([[subQ4,1.0]])],"derivedFrom":subQ3}),1.0]])]});}
            var Q24;
            {var subQ1=sQuery(id+"F3.wireOp",EDGE,"E11.bottom");var subQ3=sQuery(id+"F3.wireOp",EDGE,"E27");var subQ4=makeQuery(id+"F3.imprint","INTERSECT",VERTEX,{"derivedFrom":[subQ1,subQ3]});Q24=makeQuery(id+"F3.imprint","IMPRINT",FACE,{"disambiguationData":[TD([[makeQuery(id+"F3.imprint","IMPRINT",EDGE,{"disambiguationData":[TD([[subQ4,1.0]])],"derivedFrom":subQ3}),1.0]])]});}
            extrude(context, id + "F4", {"entities" : qUnion([Q0, Q1, Q2, Q3, Q4, Q5, Q6, Q7, Q8, Q9, Q10, Q11, Q12, Q13, Q14, Q15, Q16, Q17, Q18, Q19, Q20, Q21, Q22, Q23, Q24]), "operationType" : NewBodyOperationType.REMOVE, "oppositeDirection" : true, "depth" : 3 * mm});
        }
        {
            var Q0;
            Q0=makeQuery(id+"F2.opExtrude","CAP_FACE",FACE,{"disambiguationData":[OSD([sQuery(id+"F0.wireOp",EDGE,"E0.bottom"),sQuery(id+"F0.wireOp",EDGE,"E0.top"),sQuery(id+"F0.wireOp",EDGE,"E0.left"),sQuery(id+"F0.wireOp",EDGE,"E0.right"),sQuery(id+"F0.wireOp",EDGE,"E3"),sQuery(id+"F0.wireOp",EDGE,"E4"),sQuery(id+"F0.wireOp",EDGE,"E5"),sQuery(id+"F0.wireOp",EDGE,"E6"),sQuery(id+"F0.wireOp",EDGE,"E7.0"),sQuery(id+"F0.wireOp",EDGE,"E8.0"),sQuery(id+"F0.wireOp",EDGE,"E9.0"),sQuery(id+"F0.wireOp",EDGE,"E10.0")])],"isStart":false});
            var sketch = newSketch(context, id + "F5", { "sketchPlane" : qUnion([Q0])});
            skLineSegment(sketch, "E28.bottom", {"start": v(-8.5, 23.5) * mm, "end": v(-7.5, 23.5) * mm});
            skLineSegment(sketch, "E28.top", {"start": v(-8.5, 22.5) * mm, "end": v(-7.5, 22.5) * mm});
            skLineSegment(sketch, "E28.left", {"start": v(-8.5, 23.5) * mm, "end": v(-8.5, 22.5) * mm});
            skLineSegment(sketch, "E28.right", {"start": v(-7.5, 23.5) * mm, "end": v(-7.5, 22.5) * mm});
            skLineSegment(sketch, "E29.bottom", {"start": v(-23.5, 8.5) * mm, "end": v(-22.5, 8.5) * mm});
            skLineSegment(sketch, "E29.top", {"start": v(-23.5, 7.5) * mm, "end": v(-22.5, 7.5) * mm});
            skLineSegment(sketch, "E29.left", {"start": v(-23.5, 8.5) * mm, "end": v(-23.5, 7.5) * mm});
            skLineSegment(sketch, "E29.right", {"start": v(-22.5, 8.5) * mm, "end": v(-22.5, 7.5) * mm});
            skLineSegment(sketch, "E30.bottom", {"start": v(7.5, 23.5) * mm, "end": v(8.5, 23.5) * mm});
            skLineSegment(sketch, "E30.top", {"start": v(7.5, 22.5) * mm, "end": v(8.5, 22.5) * mm});
            skLineSegment(sketch, "E30.left", {"start": v(7.5, 23.5) * mm, "end": v(7.5, 22.5) * mm});
            skLineSegment(sketch, "E30.right", {"start": v(8.5, 23.5) * mm, "end": v(8.5, 22.5) * mm});
            skLineSegment(sketch, "E31.bottom", {"start": v(23.5, 8.5) * mm, "end": v(22.5, 8.5) * mm});
            skLineSegment(sketch, "E31.top", {"start": v(23.5, 7.5) * mm, "end": v(22.5, 7.5) * mm});
            skLineSegment(sketch, "E31.left", {"start": v(23.5, 8.5) * mm, "end": v(23.5, 7.5) * mm});
            skLineSegment(sketch, "E31.right", {"start": v(22.5, 8.5) * mm, "end": v(22.5, 7.5) * mm});
            skLineSegment(sketch, "E32.bottom", {"start": v(23.5, -7.5) * mm, "end": v(22.5, -7.5) * mm});
            skLineSegment(sketch, "E32.top", {"start": v(23.5, -8.5) * mm, "end": v(22.5, -8.5) * mm});
            skLineSegment(sketch, "E32.left", {"start": v(23.5, -7.5) * mm, "end": v(23.5, -8.5) * mm});
            skLineSegment(sketch, "E32.right", {"start": v(22.5, -7.5) * mm, "end": v(22.5, -8.5) * mm});
            skLineSegment(sketch, "E33.bottom", {"start": v(8.5, -23.5) * mm, "end": v(7.5, -23.5) * mm});
            skLineSegment(sketch, "E33.top", {"start": v(8.5, -22.5) * mm, "end": v(7.5, -22.5) * mm});
            skLineSegment(sketch, "E33.left", {"start": v(8.5, -23.5) * mm, "end": v(8.5, -22.5) * mm});
            skLineSegment(sketch, "E33.right", {"start": v(7.5, -23.5) * mm, "end": v(7.5, -22.5) * mm});
            skLineSegment(sketch, "E34.bottom", {"start": v(-7.5, -23.5) * mm, "end": v(-8.5, -23.5) * mm});
            skLineSegment(sketch, "E34.top", {"start": v(-7.5, -22.5) * mm, "end": v(-8.5, -22.5) * mm});
            skLineSegment(sketch, "E34.left", {"start": v(-7.5, -23.5) * mm, "end": v(-7.5, -22.5) * mm});
            skLineSegment(sketch, "E34.right", {"start": v(-8.5, -23.5) * mm, "end": v(-8.5, -22.5) * mm});
            skLineSegment(sketch, "E35.bottom", {"start": v(-23.5, -8.5) * mm, "end": v(-22.5, -8.5) * mm});
            skLineSegment(sketch, "E35.top", {"start": v(-23.5, -7.5) * mm, "end": v(-22.5, -7.5) * mm});
            skLineSegment(sketch, "E35.left", {"start": v(-23.5, -8.5) * mm, "end": v(-23.5, -7.5) * mm});
            skLineSegment(sketch, "E35.right", {"start": v(-22.5, -8.5) * mm, "end": v(-22.5, -7.5) * mm});
            skSolve(sketch);
        }
        {
            var Q0;
            Q0=qSketchRegion(id+"F5",true);
            extrude(context, id + "F6", {"entities" : qUnion([Q0]), "operationType" : NewBodyOperationType.REMOVE, "oppositeDirection" : true, "depth" : 25 * mm});
        }
        {
            var Q0;
            Q0=qSketchRegion(id+"F5",true);
            extrude(context, id + "F7", {"entities" : qUnion([Q0]), "operationType" : NewBodyOperationType.ADD, "oppositeDirection" : true, "depth" : 15 * mm});
        }
        {
            var Q0;
            Q0=qCreatedBy(makeId("Top.planeOp"),FACE);
            var sketch = newSketch(context, id + "F8", { "sketchPlane" : qUnion([Q0])});
            skPoint(sketch, "E36.0", {"position": v(-7.5, 7.5) * mm});
            skPoint(sketch, "E37.0", {"position": v(7.5, -7.5) * mm});
            skLineSegment(sketch, "E38.bottom", {"start": v(-7.5, 7.5) * mm, "end": v(7.5, 7.5) * mm});
            skLineSegment(sketch, "E38.top", {"start": v(-7.5, -7.5) * mm, "end": v(7.5, -7.5) * mm});
            skLineSegment(sketch, "E38.left", {"start": v(-7.5, 7.5) * mm, "end": v(-7.5, -7.5) * mm});
            skLineSegment(sketch, "E38.right", {"start": v(7.5, 7.5) * mm, "end": v(7.5, -7.5) * mm});
            skLineSegment(sketch, "E39.bottom", {"start": v(-7.5, 7.5) * mm, "end": v(-5.5, 7.5) * mm});
            skLineSegment(sketch, "E39.top", {"start": v(-7.5, 5.5) * mm, "end": v(-5.5, 5.5) * mm});
            skLineSegment(sketch, "E39.left", {"start": v(-7.5, 7.5) * mm, "end": v(-7.5, 5.5) * mm});
            skLineSegment(sketch, "E39.right", {"start": v(-5.5, 7.5) * mm, "end": v(-5.5, 5.5) * mm});
            skLineSegment(sketch, "E40.bottom", {"start": v(7.5, 7.5) * mm, "end": v(5.5, 7.5) * mm});
            skLineSegment(sketch, "E40.top", {"start": v(7.5, 5.5) * mm, "end": v(5.5, 5.5) * mm});
            skLineSegment(sketch, "E40.left", {"start": v(7.5, 7.5) * mm, "end": v(7.5, 5.5) * mm});
            skLineSegment(sketch, "E40.right", {"start": v(5.5, 7.5) * mm, "end": v(5.5, 5.5) * mm});
            skLineSegment(sketch, "E41.bottom", {"start": v(7.5, -7.5) * mm, "end": v(5.5, -7.5) * mm});
            skLineSegment(sketch, "E41.top", {"start": v(7.5, -5.5) * mm, "end": v(5.5, -5.5) * mm});
            skLineSegment(sketch, "E41.left", {"start": v(7.5, -7.5) * mm, "end": v(7.5, -5.5) * mm});
            skLineSegment(sketch, "E41.right", {"start": v(5.5, -7.5) * mm, "end": v(5.5, -5.5) * mm});
            skLineSegment(sketch, "E42.bottom", {"start": v(-7.5, -7.5) * mm, "end": v(-5.5, -7.5) * mm});
            skLineSegment(sketch, "E42.top", {"start": v(-7.5, -5.5) * mm, "end": v(-5.5, -5.5) * mm});
            skLineSegment(sketch, "E42.left", {"start": v(-7.5, -7.5) * mm, "end": v(-7.5, -5.5) * mm});
            skLineSegment(sketch, "E42.right", {"start": v(-5.5, -7.5) * mm, "end": v(-5.5, -5.5) * mm});
            skPoint(sketch, "E43.0", {"position": v(8.5, 1) * mm});
            skPoint(sketch, "E44.0", {"position": v(8.5, -1) * mm});
            skLineSegment(sketch, "E45.bottom", {"start": v(7.5, 1) * mm, "end": v(5.5, 1) * mm});
            skLineSegment(sketch, "E45.top", {"start": v(7.5, -1) * mm, "end": v(5.5, -1) * mm});
            skLineSegment(sketch, "E45.left", {"start": v(8.5, 1) * mm, "end": v(8.5, -1) * mm});
            skLineSegment(sketch, "E45.right", {"start": v(-7.5, 1) * mm, "end": v(-7.5, -1) * mm});
            skLineSegment(sketch, "E46.0.0", {"start": v(-7.5, 8.5) * mm, "end": v(-7.5, 23.5) * mm, "construction": true});
            skLineSegment(sketch, "E46.0.1", {"start": v(-7.5, 23.5) * mm, "end": v(-8.5, 23.5) * mm, "construction": true});
            skLineSegment(sketch, "E46.0.2", {"start": v(-8.5, 23.5) * mm, "end": v(-8.5, 8.5) * mm, "construction": true});
            skLineSegment(sketch, "E46.0.3", {"start": v(-8.5, 8.5) * mm, "end": v(-23.5, 8.5) * mm, "construction": true});
            skLineSegment(sketch, "E46.0.4", {"start": v(-23.5, 8.5) * mm, "end": v(-23.5, 7.5) * mm, "construction": true});
            skLineSegment(sketch, "E46.0.5", {"start": v(-23.5, 7.5) * mm, "end": v(-8.5, 7.5) * mm, "construction": true});
            skLineSegment(sketch, "E46.0.6", {"start": v(-8.5, 7.5) * mm, "end": v(-8.5, -7.5) * mm, "construction": true});
            skLineSegment(sketch, "E46.0.7", {"start": v(-8.5, -7.5) * mm, "end": v(-23.5, -7.5) * mm, "construction": true});
            skLineSegment(sketch, "E46.0.8", {"start": v(-23.5, -7.5) * mm, "end": v(-23.5, -8.5) * mm, "construction": true});
            skLineSegment(sketch, "E46.0.9", {"start": v(-23.5, -8.5) * mm, "end": v(-8.5, -8.5) * mm, "construction": true});
            skLineSegment(sketch, "E46.0.10", {"start": v(-8.5, -8.5) * mm, "end": v(-8.5, -23.5) * mm, "construction": true});
            skLineSegment(sketch, "E46.0.11", {"start": v(-8.5, -23.5) * mm, "end": v(-7.5, -23.5) * mm, "construction": true});
            skLineSegment(sketch, "E46.0.12", {"start": v(-7.5, -23.5) * mm, "end": v(-7.5, -8.5) * mm, "construction": true});
            skLineSegment(sketch, "E46.0.13", {"start": v(-7.5, -8.5) * mm, "end": v(7.5, -8.5) * mm, "construction": true});
            skLineSegment(sketch, "E46.0.14", {"start": v(7.5, -8.5) * mm, "end": v(7.5, -23.5) * mm, "construction": true});
            skLineSegment(sketch, "E46.0.15", {"start": v(7.5, -23.5) * mm, "end": v(8.5, -23.5) * mm, "construction": true});
            skLineSegment(sketch, "E46.0.16", {"start": v(8.5, -23.5) * mm, "end": v(8.5, -8.5) * mm, "construction": true});
            skLineSegment(sketch, "E46.0.17", {"start": v(8.5, -8.5) * mm, "end": v(23.5, -8.5) * mm, "construction": true});
            skLineSegment(sketch, "E46.0.18", {"start": v(23.5, -8.5) * mm, "end": v(23.5, -7.5) * mm, "construction": true});
            skLineSegment(sketch, "E46.0.19", {"start": v(23.5, -7.5) * mm, "end": v(8.5, -7.5) * mm, "construction": true});
            skLineSegment(sketch, "E46.0.20", {"start": v(8.5, -7.5) * mm, "end": v(8.5, 7.5) * mm, "construction": true});
            skLineSegment(sketch, "E46.0.21", {"start": v(8.5, 7.5) * mm, "end": v(23.5, 7.5) * mm, "construction": true});
            skLineSegment(sketch, "E46.0.22", {"start": v(23.5, 7.5) * mm, "end": v(23.5, 8.5) * mm, "construction": true});
            skLineSegment(sketch, "E46.0.23", {"start": v(23.5, 8.5) * mm, "end": v(8.5, 8.5) * mm, "construction": true});
            skLineSegment(sketch, "E46.0.24", {"start": v(8.5, 8.5) * mm, "end": v(8.5, 23.5) * mm, "construction": true});
            skLineSegment(sketch, "E46.0.25", {"start": v(8.5, 23.5) * mm, "end": v(7.5, 23.5) * mm, "construction": true});
            skLineSegment(sketch, "E46.0.26", {"start": v(7.5, 23.5) * mm, "end": v(7.5, 8.5) * mm, "construction": true});
            skLineSegment(sketch, "E46.0.27", {"start": v(7.5, 8.5) * mm, "end": v(-7.5, 8.5) * mm, "construction": true});
            skLineSegment(sketch, "E47.0.20", {"start": v(8.5, -7.5) * mm, "end": v(8.5, -1) * mm, "construction": true});
            skLineSegment(sketch, "E48", {"start": v(7.5, 1) * mm, "end": v(7.5, -1) * mm});
            skLineSegment(sketch, "E49.trimOffspring", {"start": v(8.5, 1) * mm, "end": v(8.5, 7.5) * mm, "construction": true});
            skLineSegment(sketch, "E50.0", {"start": v(-6.5, 1) * mm, "end": v(-6.5, -1) * mm});
            skLineSegment(sketch, "E51.0", {"start": v(5.5, 1) * mm, "end": v(5.5, -1) * mm});
            skLineSegment(sketch, "E52.trimOffspring", {"start": v(-6.5, -1) * mm, "end": v(-7.5, -1) * mm});
            skLineSegment(sketch, "E53.trimOffspring", {"start": v(-6.5, 1) * mm, "end": v(-7.5, 1) * mm});
            skLineSegment(sketch, "E54.bottom", {"start": v(-1, 7.5) * mm, "end": v(1, 7.5) * mm});
            skLineSegment(sketch, "E54.top", {"start": v(-1, 5.5) * mm, "end": v(1, 5.5) * mm});
            skLineSegment(sketch, "E54.left", {"start": v(-1, 7.5) * mm, "end": v(-1, 5.5) * mm});
            skLineSegment(sketch, "E54.right", {"start": v(1, 7.5) * mm, "end": v(1, 5.5) * mm});
            skLineSegment(sketch, "E55.bottom", {"start": v(-1, -7.5) * mm, "end": v(1, -7.5) * mm});
            skLineSegment(sketch, "E55.top", {"start": v(-1, -5.5) * mm, "end": v(1, -5.5) * mm});
            skLineSegment(sketch, "E55.left", {"start": v(-1, -7.5) * mm, "end": v(-1, -5.5) * mm});
            skLineSegment(sketch, "E55.right", {"start": v(1, -7.5) * mm, "end": v(1, -5.5) * mm});
            skLineSegment(sketch, "E56", {"start": v(0, 7.5) * mm, "end": v(0, -7.5) * mm, "construction": true});
            skSolve(sketch);
        }
        {
            var Q0;
            Q0=makeQuery(id+"F8.imprint","IMPRINT",FACE,{"disambiguationData":[TD([[makeQuery(id+"F8.imprint","IMPRINT",EDGE,{"derivedFrom":sQuery(id+"F8.wireOp",EDGE,"E38.bottom")}),-1.0]])]});
            extrude(context, id + "F9", {"entities" : qUnion([Q0]), "operationType" : NewBodyOperationType.ADD, "depth" : 1 * mm});
        }
    });
